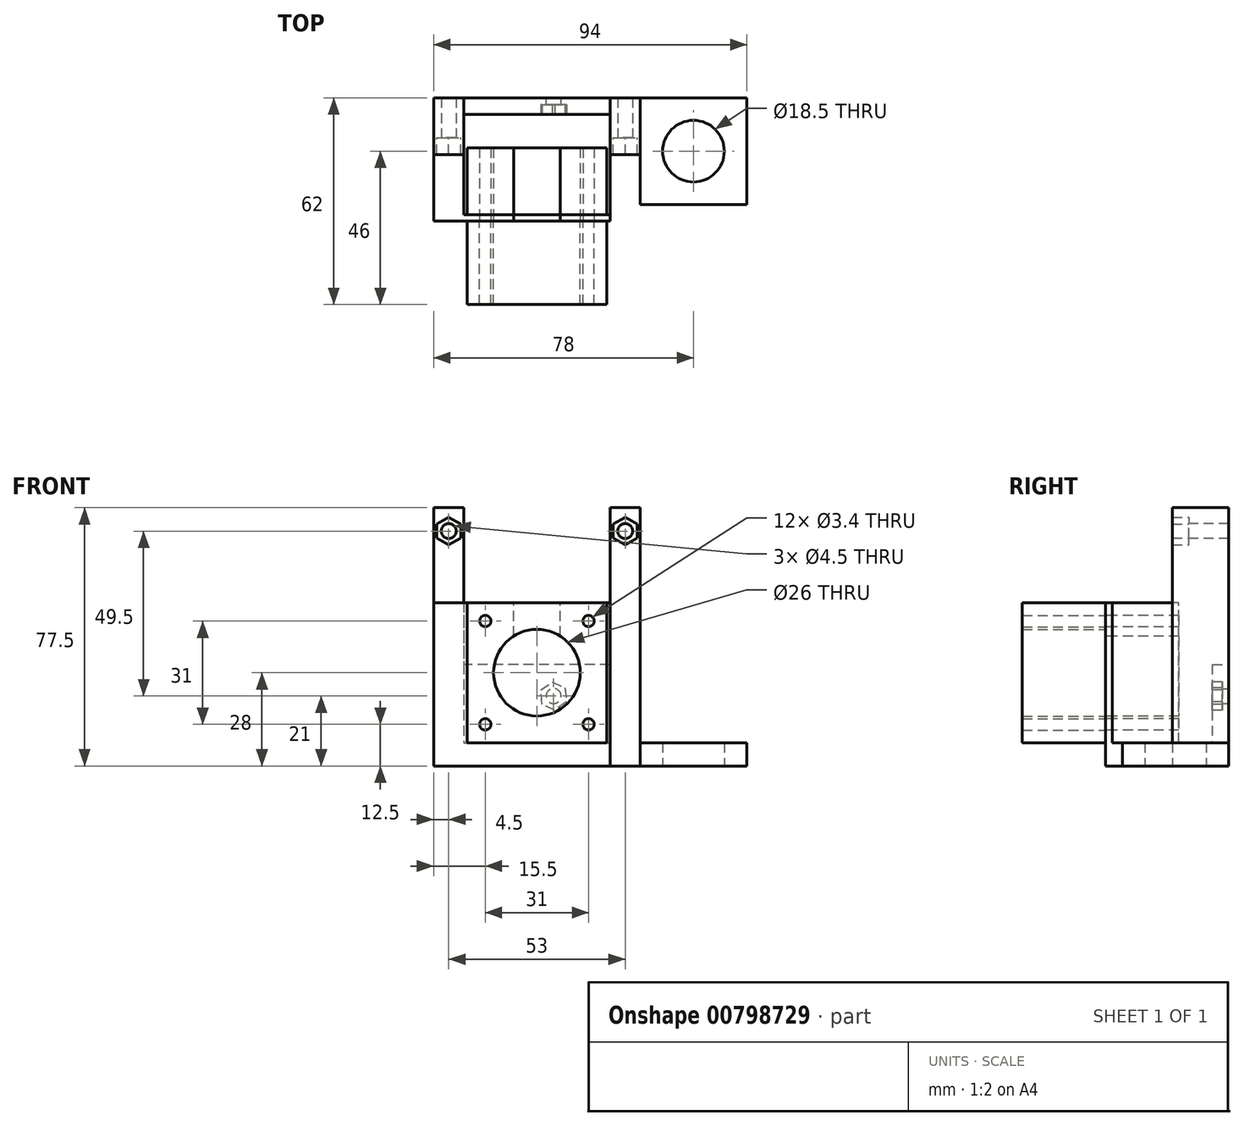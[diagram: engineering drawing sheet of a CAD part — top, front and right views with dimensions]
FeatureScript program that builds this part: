
annotation { "Feature Type Name" : "Feature", "Feature Type Description" : "" }
export const myFeature = defineFeature(function(context is Context, id is Id, definition is map)
    precondition{}
    {
        {
            assignVariable(context, id + "F0", {"name" : "MotorLength", "anyValue" : 20});
        }
        {
            var Q0;
            Q0=qCreatedBy(makeId("Front.planeOp"),FACE);
            var sketch = newSketch(context, id + "F1", { "sketchPlane" : qUnion([Q0])});
            skCircle(sketch, "E0", {"center": v(0, 0) * mm, "radius": 2.25 * mm});
            skCircle(sketch, "E1", {"center": v(-31.5, 49.5) * mm, "radius": 2.25 * mm});
            skCircle(sketch, "E2", {"center": v(21.5, 49.5) * mm, "radius": 2.25 * mm});
            skPoint(sketch, "E3", {"position": v(-36, 56.5) * mm});
            skPoint(sketch, "E4", {"position": v(-27, 56.5) * mm});
            skPoint(sketch, "E5", {"position": v(-27, -14) * mm});
            skLineSegment(sketch, "E6", {"start": v(-36, 56.5) * mm, "end": v(-27, 56.5) * mm});
            skLineSegment(sketch, "E7", {"start": v(-27, 56.5) * mm, "end": v(-27, -14) * mm});
            skLineSegment(sketch, "E8", {"start": v(-27, -14) * mm, "end": v(17, -14) * mm});
            skLineSegment(sketch, "E9", {"start": v(17, -14) * mm, "end": v(17, 56.5) * mm});
            skLineSegment(sketch, "E10", {"start": v(17, 56.5) * mm, "end": v(26, 56.5) * mm});
            skPoint(sketch, "E11", {"position": v(-36, -21) * mm});
            skLineSegment(sketch, "E12", {"start": v(-36, 56.5) * mm, "end": v(-36, -21) * mm});
            skLineSegment(sketch, "E13", {"start": v(-36, -21) * mm, "end": v(26, -21) * mm});
            skLineSegment(sketch, "E14", {"start": v(26, 56.5) * mm, "end": v(26, -21) * mm});
            skSolve(sketch);
        }
        {
            var Q0;
            Q0=makeQuery(id+"F1.imprint","IMPRINT",FACE,{"disambiguationData":[TD([[makeQuery(id+"F1.imprint","IMPRINT",EDGE,{"derivedFrom":sQuery(id+"F1.wireOp",EDGE,"E1")}),-1.0]])]});
            extrude(context, id + "F2", {"entities" : qUnion([Q0]), "oppositeDirection" : true, "depth" : 12 * mm});
        }
        {
            var Q0;
            Q0=makeQuery(id+"F2.opExtrude","CAP_FACE",FACE,{"disambiguationData":[OSD([sQuery(id+"F1.wireOp",EDGE,"E1"),sQuery(id+"F1.wireOp",EDGE,"E2"),sQuery(id+"F1.wireOp",EDGE,"E6"),sQuery(id+"F1.wireOp",EDGE,"E7"),sQuery(id+"F1.wireOp",EDGE,"E8"),sQuery(id+"F1.wireOp",EDGE,"E9"),sQuery(id+"F1.wireOp",EDGE,"E10"),sQuery(id+"F1.wireOp",EDGE,"E12"),sQuery(id+"F1.wireOp",EDGE,"E13"),sQuery(id+"F1.wireOp",EDGE,"E14")])],"isStart":true});
            var sketch = newSketch(context, id + "F3", { "sketchPlane" : qUnion([Q0])});
            skCircle(sketch, "E15.cCircle", {"center": v(-31.5, 49.5) * mm, "radius": 3.6 * mm, "construction": true});
            skLineSegment(sketch, "E15.0", {"start": v(-27.9, 51.58) * mm, "end": v(-27.9, 47.42) * mm});
            skLineSegment(sketch, "E15.1", {"start": v(-27.9, 47.42) * mm, "end": v(-31.5, 45.34) * mm});
            skLineSegment(sketch, "E15.2", {"start": v(-31.5, 45.34) * mm, "end": v(-35.1, 47.42) * mm});
            skLineSegment(sketch, "E15.3", {"start": v(-35.1, 47.42) * mm, "end": v(-35.1, 51.58) * mm});
            skLineSegment(sketch, "E15.4", {"start": v(-35.1, 51.58) * mm, "end": v(-31.5, 53.66) * mm});
            skLineSegment(sketch, "E15.5", {"start": v(-31.5, 53.66) * mm, "end": v(-27.9, 51.58) * mm});
            skPoint(sketch, "E15.0.midPoint", {"position": v(-27.9, 49.5) * mm});
            skCircle(sketch, "E16.cCircle", {"center": v(21.5, 49.5) * mm, "radius": 3.6 * mm, "construction": true});
            skLineSegment(sketch, "E16.0", {"start": v(25.1, 51.58) * mm, "end": v(25.1, 47.42) * mm});
            skLineSegment(sketch, "E16.1", {"start": v(25.1, 47.42) * mm, "end": v(21.5, 45.34) * mm});
            skLineSegment(sketch, "E16.2", {"start": v(21.5, 45.34) * mm, "end": v(17.9, 47.42) * mm});
            skLineSegment(sketch, "E16.3", {"start": v(17.9, 47.42) * mm, "end": v(17.9, 51.58) * mm});
            skLineSegment(sketch, "E16.4", {"start": v(17.9, 51.58) * mm, "end": v(21.5, 53.66) * mm});
            skLineSegment(sketch, "E16.5", {"start": v(21.5, 53.66) * mm, "end": v(25.1, 51.58) * mm});
            skPoint(sketch, "E16.0.midPoint", {"position": v(25.1, 49.5) * mm});
            skSolve(sketch);
        }
        {
            var Q0;
            Q0=makeQuery(id+"F3.imprint","IMPRINT",FACE,{"disambiguationData":[TD([[makeQuery(id+"F3.imprint","IMPRINT",EDGE,{"derivedFrom":sQuery(id+"F3.wireOp",EDGE,"E15.0")}),1.0]])]});
            extrude(context, id + "F4", {"entities" : qUnion([Q0]), "operationType" : NewBodyOperationType.ADD, "depth" : 5 * mm});
        }
        {
            var Q0;
            {var subQ0=sQuery(id+"F1.wireOp",EDGE,"E8");Q0=makeQuery(id+"F4.boolean.opBoolean","MERGE",FACE,{"derivedFrom":[makeQuery(id+"F2.opExtrude","SWEPT_FACE",FACE,{"disambiguationData":[OSD([subQ0])]}),makeQuery(id+"F4.opExtrude","SWEPT_FACE",FACE,{"disambiguationData":[OSD([subQ0])]})]});}
            var sketch = newSketch(context, id + "F5", { "sketchPlane" : qUnion([Q0])});
            skLineSegment(sketch, "E17.0", {"start": v(-27, 12) * mm, "end": v(17, 12) * mm});
            skPoint(sketch, "E18.oppositeSnap0", {"position": v(17, 3.5) * mm});
            skLineSegment(sketch, "E18.top", {"start": v(-27, -23) * mm, "end": v(17, -23) * mm});
            skLineSegment(sketch, "E18.left", {"start": v(-27, 12) * mm, "end": v(-27, -23) * mm});
            skLineSegment(sketch, "E18.right", {"start": v(17, 12) * mm, "end": v(17, -23) * mm});
            skLineSegment(sketch, "E19.top", {"start": v(-27, -25) * mm, "end": v(17, -25) * mm});
            skLineSegment(sketch, "E19.left", {"start": v(-27, -23) * mm, "end": v(-27, -25) * mm});
            skLineSegment(sketch, "E19.right", {"start": v(17, -23) * mm, "end": v(17, -25) * mm});
            skLineSegment(sketch, "E20.0", {"start": v(17, -5) * mm, "end": v(26, -5) * mm});
            skLineSegment(sketch, "E21.bottom", {"start": v(26, -5) * mm, "end": v(17, -5) * mm});
            skLineSegment(sketch, "E21.top", {"start": v(26, -25) * mm, "end": v(17, -25) * mm});
            skLineSegment(sketch, "E21.left", {"start": v(26, -5) * mm, "end": v(26, -25) * mm});
            skLineSegment(sketch, "E21.right", {"start": v(17, -5) * mm, "end": v(17, -25) * mm});
            skLineSegment(sketch, "E22.0", {"start": v(-36, -5) * mm, "end": v(-27, -5) * mm});
            skLineSegment(sketch, "E23.top", {"start": v(-36, -25) * mm, "end": v(-27, -25) * mm});
            skLineSegment(sketch, "E23.left", {"start": v(-36, -5) * mm, "end": v(-36, -25) * mm});
            skLineSegment(sketch, "E23.right", {"start": v(-27, -5) * mm, "end": v(-27, -25) * mm});
            skSolve(sketch);
        }
        {
            var Q0;
            {var subQ0=sQuery(id+"F5.wireOp",EDGE,"E18.top");Q0=makeQuery(id+"F5.imprint","IMPRINT",FACE,{"disambiguationData":[TD([[makeQuery(id+"F5.imprint","IMPRINT",EDGE,{"derivedFrom":subQ0}),1.0]])]});}
            var Q1;
            {var subQ0=sQuery(id+"F5.wireOp",EDGE,"E18.top");Q1=makeQuery(id+"F5.imprint","IMPRINT",FACE,{"disambiguationData":[TD([[makeQuery(id+"F5.imprint","IMPRINT",EDGE,{"derivedFrom":subQ0}),-1.0]])]});}
            var Q2;
            {var subQ1=sQuery(id+"F5.wireOp",EDGE,"E22.0");Q2=makeQuery(id+"F5.imprint","IMPRINT",FACE,{"disambiguationData":[TD([[makeQuery(id+"F5.imprint","IMPRINT",EDGE,{"derivedFrom":subQ1}),-1.0]])]});}
            var Q3;
            {var subQ1=sQuery(id+"F5.wireOp",EDGE,"E21.bottom");Q3=makeQuery(id+"F5.imprint","IMPRINT",FACE,{"disambiguationData":[TD([[makeQuery(id+"F5.imprint","IMPRINT",EDGE,{"derivedFrom":subQ1}),1.0]])]});}
            var Q4;
            {var subQ0=sQuery(id+"F1.wireOp",EDGE,"E13");Q4=makeQuery(id+"F4.boolean.opBoolean","MERGE",FACE,{"derivedFrom":[makeQuery(id+"F2.opExtrude","SWEPT_FACE",FACE,{"disambiguationData":[OSD([subQ0])]}),makeQuery(id+"F4.opExtrude","SWEPT_FACE",FACE,{"disambiguationData":[OSD([subQ0])]})]});}
            extrude(context, id + "F6", {"entities" : qUnion([Q0, Q1, Q2, Q3]), "operationType" : NewBodyOperationType.ADD, "endBound" : BoundingType.UP_TO_SURFACE, "oppositeDirection" : true, "endBoundEntityFace" : qUnion([Q4]), "depth" : 25 * mm});
        }
        {
            var Q0;
            {var subQ0=sQuery(id+"F5.wireOp",EDGE,"E18.top");Q0=makeQuery(id+"F5.imprint","IMPRINT",FACE,{"disambiguationData":[TD([[makeQuery(id+"F5.imprint","IMPRINT",EDGE,{"derivedFrom":subQ0}),-1.0]])]});}
            var Q1;
            {var subQ1=sQuery(id+"F5.wireOp",EDGE,"E22.0");Q1=makeQuery(id+"F5.imprint","IMPRINT",FACE,{"disambiguationData":[TD([[makeQuery(id+"F5.imprint","IMPRINT",EDGE,{"derivedFrom":subQ1}),-1.0]])]});}
            var Q2;
            {var subQ1=sQuery(id+"F5.wireOp",EDGE,"E21.bottom");Q2=makeQuery(id+"F5.imprint","IMPRINT",FACE,{"disambiguationData":[TD([[makeQuery(id+"F5.imprint","IMPRINT",EDGE,{"derivedFrom":subQ1}),1.0]])]});}
            extrude(context, id + "F7", {"entities" : qUnion([Q0, Q1, Q2]), "operationType" : NewBodyOperationType.ADD, "depth" : 42 * mm});
        }
        {
            var Q0;
            {var subQ0=sQuery(id+"F5.wireOp",EDGE,"E23.top");var subQ1=sQuery(id+"F5.wireOp",EDGE,"E21.top");var subQ2=sQuery(id+"F5.wireOp",EDGE,"E19.top");Q0=makeQuery(id+"F7.boolean.opBoolean","MERGE",FACE,{"derivedFrom":[makeQuery(id+"F6.opExtrude","SWEPT_FACE",FACE,{"disambiguationData":[OSD([subQ2,subQ1,subQ0])]}),makeQuery(id+"F7.opExtrude","SWEPT_FACE",FACE,{"disambiguationData":[OSD([subQ2,subQ1,subQ0])]})]});}
            var sketch = newSketch(context, id + "F8", { "sketchPlane" : qUnion([Q0])});
            skLineSegment(sketch, "E24.0", {"start": v(-26, -14) * mm, "end": v(16, -14) * mm});
            skPoint(sketch, "E25", {"position": v(-5, -14) * mm});
            skPoint(sketch, "E26", {"position": v(-26, -14) * mm});
            skPoint(sketch, "E27", {"position": v(16, -14) * mm});
            skPoint(sketch, "E28.orphan", {"position": v(-27, -14) * mm});
            skPoint(sketch, "E29.orphan", {"position": v(17, -14) * mm});
            skPoint(sketch, "E30", {"position": v(-26, 28) * mm});
            skPoint(sketch, "E31", {"position": v(16, 28) * mm});
            skLineSegment(sketch, "E32", {"start": v(-26, 28) * mm, "end": v(16, -14) * mm, "construction": true});
            skLineSegment(sketch, "E33", {"start": v(-26, -14) * mm, "end": v(16, 28) * mm, "construction": true});
            skPoint(sketch, "E34", {"position": v(-5, 7) * mm});
            skCircle(sketch, "E35", {"center": v(-5, 7) * mm, "radius": 13 * mm});
            skCircle(sketch, "E36", {"center": v(-20.5, 22.5) * mm, "radius": 1.7 * mm});
            skCircle(sketch, "E37.1.0", {"center": v(-20.5, -8.5) * mm, "radius": 1.7 * mm});
            skCircle(sketch, "E37.2.0", {"center": v(10.5, -8.5) * mm, "radius": 1.7 * mm});
            skCircle(sketch, "E37.3.0", {"center": v(10.5, 22.5) * mm, "radius": 1.7 * mm});
            skSolve(sketch);
        }
        {
            var Q0;
            Q0=makeQuery(id+"F8.imprint","IMPRINT",FACE,{"disambiguationData":[TD([[makeQuery(id+"F8.imprint","IMPRINT",EDGE,{"derivedFrom":sQuery(id+"F8.wireOp",EDGE,"E36")}),1.0]])]});
            var Q1;
            Q1=makeQuery(id+"F8.imprint","IMPRINT",FACE,{"disambiguationData":[TD([[makeQuery(id+"F8.imprint","IMPRINT",EDGE,{"derivedFrom":sQuery(id+"F8.wireOp",EDGE,"E35")}),1.0]])]});
            var Q2;
            Q2=makeQuery(id+"F8.imprint","IMPRINT",FACE,{"disambiguationData":[TD([[makeQuery(id+"F8.imprint","IMPRINT",EDGE,{"derivedFrom":sQuery(id+"F8.wireOp",EDGE,"E37.1.0")}),1.0]])]});
            var Q3;
            Q3=makeQuery(id+"F8.imprint","IMPRINT",FACE,{"disambiguationData":[TD([[makeQuery(id+"F8.imprint","IMPRINT",EDGE,{"derivedFrom":sQuery(id+"F8.wireOp",EDGE,"E37.2.0")}),1.0]])]});
            var Q4;
            Q4=makeQuery(id+"F8.imprint","IMPRINT",FACE,{"disambiguationData":[TD([[makeQuery(id+"F8.imprint","IMPRINT",EDGE,{"derivedFrom":sQuery(id+"F8.wireOp",EDGE,"E37.3.0")}),1.0]])]});
            var Q5;
            Q5=makeQuery(id+"F7.opExtrude","SWEPT_FACE",FACE,{"disambiguationData":[OSD([sQuery(id+"F5.wireOp",EDGE,"E18.top")])]});
            extrude(context, id + "F9", {"entities" : qUnion([Q0, Q1, Q2, Q3, Q4]), "operationType" : NewBodyOperationType.REMOVE, "endBound" : BoundingType.UP_TO_SURFACE, "oppositeDirection" : true, "endBoundEntityFace" : qUnion([Q5]), "depth" : 25 * mm});
        }
        {
            var Q0;
            Q0=makeQuery(id+"F7.opExtrude","CAP_FACE",FACE,{"disambiguationData":[OSD([sQuery(id+"F5.wireOp",EDGE,"E18.top"),sQuery(id+"F5.wireOp",EDGE,"E19.top"),sQuery(id+"F5.wireOp",EDGE,"E21.bottom"),sQuery(id+"F5.wireOp",EDGE,"E21.top"),sQuery(id+"F5.wireOp",EDGE,"E21.left"),sQuery(id+"F5.wireOp",EDGE,"E21.right"),sQuery(id+"F5.wireOp",EDGE,"E22.0"),sQuery(id+"F5.wireOp",EDGE,"E23.top"),sQuery(id+"F5.wireOp",EDGE,"E23.left"),sQuery(id+"F5.wireOp",EDGE,"E23.right")])],"isStart":false});
            var sketch = newSketch(context, id + "F10", { "sketchPlane" : qUnion([Q0])});
            skLineSegment(sketch, "E38", {"start": v(-5, -25) * mm, "end": v(-5, -23) * mm, "construction": true});
            skLineSegment(sketch, "E39", {"start": v(-5, -23) * mm, "end": v(-12, -23) * mm});
            skLineSegment(sketch, "E40", {"start": v(-5, -23) * mm, "end": v(2, -23) * mm});
            skLineSegment(sketch, "E41.bottom", {"start": v(-12, -23) * mm, "end": v(2, -23) * mm});
            skLineSegment(sketch, "E41.top", {"start": v(-12, -25) * mm, "end": v(2, -25) * mm});
            skLineSegment(sketch, "E41.left", {"start": v(-12, -23) * mm, "end": v(-12, -25) * mm});
            skLineSegment(sketch, "E41.right", {"start": v(2, -23) * mm, "end": v(2, -25) * mm});
            skSolve(sketch);
        }
        {
            var Q0;
            Q0=makeQuery(id+"F10.imprint","IMPRINT",FACE,{"disambiguationData":[TD([[makeQuery(id+"F10.imprint","IMPRINT",EDGE,{"derivedFrom":sQuery(id+"F10.wireOp",EDGE,"E41.top")}),1.0]])]});
            var Q1;
            Q1=makeQuery(id+"F9.boolean.opBoolean","COPY",FACE,{"derivedFrom":makeQuery(id+"F9.opExtrude","SWEPT_FACE",FACE,{"disambiguationData":[OSD([sQuery(id+"F8.wireOp",EDGE,"E35")])]})});
            extrude(context, id + "F11", {"entities" : qUnion([Q0]), "operationType" : NewBodyOperationType.REMOVE, "endBound" : BoundingType.UP_TO_SURFACE, "oppositeDirection" : true, "endBoundEntityFace" : qUnion([Q1]), "depth" : 25 * mm});
        }
        {
            var Q0;
            Q0=makeQuery(id+"F7.opExtrude","SWEPT_FACE",FACE,{"disambiguationData":[OSD([sQuery(id+"F5.wireOp",EDGE,"E18.top")])]});
            var sketch = newSketch(context, id + "F12", { "sketchPlane" : qUnion([Q0])});
            skLineSegment(sketch, "E42.0", {"start": v(26, -14) * mm, "end": v(-16, -14) * mm});
            skLineSegment(sketch, "E43", {"start": v(-16, -14) * mm, "end": v(-16, 28) * mm});
            skLineSegment(sketch, "E44", {"start": v(-16, 28) * mm, "end": v(26, 28) * mm});
            skLineSegment(sketch, "E45", {"start": v(26, 28) * mm, "end": v(26, -14) * mm});
            skSolve(sketch);
        }
        {
            var Q0;
            Q0=makeQuery(id+"F12.imprint","IMPRINT",FACE,{"disambiguationData":[TD([[makeQuery(id+"F12.imprint","IMPRINT",EDGE,{"derivedFrom":sQuery(id+"F12.wireOp",EDGE,"E42.0")}),-1.0]])]});
            var Q1;
            {var subQ2=sQuery(id+"F5.wireOp",EDGE,"E18.top");Q1=makeQuery(id+"F12.imprint","IMPRINT",FACE,{"disambiguationData":[TD([[makeQuery(id+"F12.imprint","IMPRINT",EDGE,{"derivedFrom":makeQuery(id+"F9.boolean.opBoolean","COPY",EDGE,{"derivedFrom":makeQuery(id+"F9.opExtrude","TWEAK_EDGE",EDGE,{"derivedFrom":[makeQuery(id+"F7.opExtrude","SWEPT_FACE",FACE,{"disambiguationData":[OSD([subQ2])]}),makeQuery(id+"F8.imprint","IMPRINT",EDGE,{"derivedFrom":sQuery(id+"F8.wireOp",EDGE,"E35")})]})})}),-1.0]])]});}
            var Q2;
            Q2=makeQuery(id+"F12.imprint","IMPRINT",FACE,{"disambiguationData":[TD([[makeQuery(id+"F12.imprint","IMPRINT",EDGE,{"derivedFrom":makeQuery(id+"F9.boolean.opBoolean","COPY",EDGE,{"derivedFrom":makeQuery(id+"F9.opExtrude","TWEAK_EDGE",EDGE,{"derivedFrom":[makeQuery(id+"F7.opExtrude","SWEPT_FACE",FACE,{"disambiguationData":[OSD([sQuery(id+"F5.wireOp",EDGE,"E18.top")])]}),makeQuery(id+"F8.imprint","IMPRINT",EDGE,{"derivedFrom":sQuery(id+"F8.wireOp",EDGE,"E36")})]})})}),-1.0]])]});
            var Q3;
            Q3=makeQuery(id+"F12.imprint","IMPRINT",FACE,{"disambiguationData":[TD([[makeQuery(id+"F12.imprint","IMPRINT",EDGE,{"derivedFrom":makeQuery(id+"F9.boolean.opBoolean","COPY",EDGE,{"derivedFrom":makeQuery(id+"F9.opExtrude","TWEAK_EDGE",EDGE,{"derivedFrom":[makeQuery(id+"F7.opExtrude","SWEPT_FACE",FACE,{"disambiguationData":[OSD([sQuery(id+"F5.wireOp",EDGE,"E18.top")])]}),makeQuery(id+"F8.imprint","IMPRINT",EDGE,{"derivedFrom":sQuery(id+"F8.wireOp",EDGE,"E37.3.0")})]})})}),-1.0]])]});
            var Q4;
            Q4=makeQuery(id+"F12.imprint","IMPRINT",FACE,{"disambiguationData":[TD([[makeQuery(id+"F12.imprint","IMPRINT",EDGE,{"derivedFrom":makeQuery(id+"F9.boolean.opBoolean","COPY",EDGE,{"derivedFrom":makeQuery(id+"F9.opExtrude","TWEAK_EDGE",EDGE,{"derivedFrom":[makeQuery(id+"F7.opExtrude","SWEPT_FACE",FACE,{"disambiguationData":[OSD([sQuery(id+"F5.wireOp",EDGE,"E18.top")])]}),makeQuery(id+"F8.imprint","IMPRINT",EDGE,{"derivedFrom":sQuery(id+"F8.wireOp",EDGE,"E37.2.0")})]})})}),-1.0]])]});
            var Q5;
            Q5=makeQuery(id+"F12.imprint","IMPRINT",FACE,{"disambiguationData":[TD([[makeQuery(id+"F12.imprint","IMPRINT",EDGE,{"derivedFrom":makeQuery(id+"F9.boolean.opBoolean","COPY",EDGE,{"derivedFrom":makeQuery(id+"F9.opExtrude","TWEAK_EDGE",EDGE,{"derivedFrom":[makeQuery(id+"F7.opExtrude","SWEPT_FACE",FACE,{"disambiguationData":[OSD([sQuery(id+"F5.wireOp",EDGE,"E18.top")])]}),makeQuery(id+"F8.imprint","IMPRINT",EDGE,{"derivedFrom":sQuery(id+"F8.wireOp",EDGE,"E37.1.0")})]})})}),-1.0]])]});
            extrude(context, id + "F13", {"entities" : qUnion([Q0, Q1, Q2, Q3, Q4, Q5]), "depth" : (getVariable(context, 'MotorLength')) * mm});
        }
        {
            var Q0;
            Q0=makeQuery(id+"F8.imprint","IMPRINT",FACE,{"disambiguationData":[TD([[makeQuery(id+"F8.imprint","IMPRINT",EDGE,{"derivedFrom":sQuery(id+"F8.wireOp",EDGE,"E35")}),-1.0]])]});
            var sketch = newSketch(context, id + "F14", { "sketchPlane" : qUnion([Q0])});
            skLineSegment(sketch, "E46.0", {"start": v(-26, 28) * mm, "end": v(16, -14) * mm, "construction": true});
            skLineSegment(sketch, "E47.0", {"start": v(-26, -14) * mm, "end": v(16, 28) * mm, "construction": true});
            skLineSegment(sketch, "E48.bottom", {"start": v(-26, 28) * mm, "end": v(16, 28) * mm});
            skLineSegment(sketch, "E48.top", {"start": v(-26, -14) * mm, "end": v(16, -14) * mm});
            skLineSegment(sketch, "E48.left", {"start": v(-26, 28) * mm, "end": v(-26, -14) * mm});
            skLineSegment(sketch, "E48.right", {"start": v(16, 28) * mm, "end": v(16, -14) * mm});
            skSolve(sketch);
        }
        {
            var Q0;
            Q0=makeQuery(id+"F14.imprint","IMPRINT",FACE,{"disambiguationData":[TD([[makeQuery(id+"F14.imprint","IMPRINT",EDGE,{"derivedFrom":sQuery(id+"F14.wireOp",EDGE,"E48.bottom")}),-1.0]])]});
            var Q1;
            Q1=makeQuery(id+"F8.imprint","IMPRINT",FACE,{"disambiguationData":[TD([[makeQuery(id+"F8.imprint","IMPRINT",EDGE,{"derivedFrom":sQuery(id+"F8.wireOp",EDGE,"E36")}),1.0]])]});
            var Q2;
            Q2=makeQuery(id+"F8.imprint","IMPRINT",FACE,{"disambiguationData":[TD([[makeQuery(id+"F8.imprint","IMPRINT",EDGE,{"derivedFrom":sQuery(id+"F8.wireOp",EDGE,"E35")}),1.0]])]});
            var Q3;
            Q3=makeQuery(id+"F8.imprint","IMPRINT",FACE,{"disambiguationData":[TD([[makeQuery(id+"F8.imprint","IMPRINT",EDGE,{"derivedFrom":sQuery(id+"F8.wireOp",EDGE,"E37.1.0")}),1.0]])]});
            var Q4;
            Q4=makeQuery(id+"F8.imprint","IMPRINT",FACE,{"disambiguationData":[TD([[makeQuery(id+"F8.imprint","IMPRINT",EDGE,{"derivedFrom":sQuery(id+"F8.wireOp",EDGE,"E37.3.0")}),1.0]])]});
            var Q5;
            Q5=makeQuery(id+"F8.imprint","IMPRINT",FACE,{"disambiguationData":[TD([[makeQuery(id+"F8.imprint","IMPRINT",EDGE,{"derivedFrom":sQuery(id+"F8.wireOp",EDGE,"E37.2.0")}),1.0]])]});
            extrude(context, id + "F15", {"entities" : qUnion([Q0, Q1, Q2, Q3, Q4, Q5]), "depth" : 25 * mm});
        }
        {
            var Q0;
            {var subQ0=sQuery(id+"F1.wireOp",EDGE,"E13");Q0=makeQuery(id+"F6.boolean.opBoolean","MERGE",FACE,{"derivedFrom":[makeQuery(id+"F4.boolean.opBoolean","MERGE",FACE,{"derivedFrom":[makeQuery(id+"F2.opExtrude","SWEPT_FACE",FACE,{"disambiguationData":[OSD([subQ0])]}),makeQuery(id+"F4.opExtrude","SWEPT_FACE",FACE,{"disambiguationData":[OSD([subQ0])]})]}),makeQuery(id+"F6.opExtrude","CAP_FACE",FACE,{"disambiguationData":[OSD([subQ0])],"isStart":false})]});}
            var sketch = newSketch(context, id + "F16", { "sketchPlane" : qUnion([Q0])});
            skLineSegment(sketch, "E49.bottom", {"start": v(26, -12) * mm, "end": v(58, -12) * mm});
            skLineSegment(sketch, "E49.top", {"start": v(26, 20) * mm, "end": v(58, 20) * mm});
            skLineSegment(sketch, "E49.left", {"start": v(26, -12) * mm, "end": v(26, 20) * mm});
            skLineSegment(sketch, "E49.right", {"start": v(58, -12) * mm, "end": v(58, 20) * mm});
            skCircle(sketch, "E50", {"center": v(42, 4) * mm, "radius": 9.25 * mm});
            skPoint(sketch, "E50.centerSnap0", {"position": v(42, -12) * mm});
            skPoint(sketch, "E50.centerSnap1", {"position": v(26, 4) * mm});
            skLineSegment(sketch, "E51.0", {"start": v(-26, 50) * mm, "end": v(-26, 25) * mm, "construction": true});
            skLineSegment(sketch, "E52.0", {"start": v(-26, 25) * mm, "end": v(16, 25) * mm, "construction": true});
            skLineSegment(sketch, "E53", {"start": v(-5, 25) * mm, "end": v(-5, 50) * mm, "construction": true});
            skLineSegment(sketch, "E54", {"start": v(6.1, 25) * mm, "end": v(6.1, 50) * mm, "construction": true});
            skPoint(sketch, "E55", {"position": v(6.1, 37.5) * mm});
            skSolve(sketch);
        }
        {
            var Q0;
            Q0=qSketchRegion(id+"F16",true);
            var Q1;
            {var subQ0=sQuery(id+"F1.wireOp",EDGE,"E8");Q1=makeQuery(id+"F6.boolean.opBoolean","MERGE",FACE,{"derivedFrom":[makeQuery(id+"F4.boolean.opBoolean","MERGE",FACE,{"derivedFrom":[makeQuery(id+"F2.opExtrude","SWEPT_FACE",FACE,{"disambiguationData":[OSD([subQ0])]}),makeQuery(id+"F4.opExtrude","SWEPT_FACE",FACE,{"disambiguationData":[OSD([subQ0])]})]}),makeQuery(id+"F6.opExtrude","CAP_FACE",FACE,{"disambiguationData":[OSD([subQ0,sQuery(id+"F5.wireOp",EDGE,"E19.top"),sQuery(id+"F5.wireOp",EDGE,"E21.bottom"),sQuery(id+"F5.wireOp",EDGE,"E21.top"),sQuery(id+"F5.wireOp",EDGE,"E21.left"),sQuery(id+"F5.wireOp",EDGE,"E22.0"),sQuery(id+"F5.wireOp",EDGE,"E23.top"),sQuery(id+"F5.wireOp",EDGE,"E23.left")])],"isStart":true})]});}
            extrude(context, id + "F17", {"entities" : qUnion([Q0]), "endBound" : BoundingType.UP_TO_SURFACE, "oppositeDirection" : true, "endBoundEntityFace" : qUnion([Q1]), "depth" : 25 * mm});
        }
        {
            var Q0;
            Q0=makeQuery(id+"F2.opExtrude","CAP_FACE",FACE,{"disambiguationData":[OSD([sQuery(id+"F1.wireOp",EDGE,"E1"),sQuery(id+"F1.wireOp",EDGE,"E2"),sQuery(id+"F1.wireOp",EDGE,"E6"),sQuery(id+"F1.wireOp",EDGE,"E7"),sQuery(id+"F1.wireOp",EDGE,"E8"),sQuery(id+"F1.wireOp",EDGE,"E9"),sQuery(id+"F1.wireOp",EDGE,"E10"),sQuery(id+"F1.wireOp",EDGE,"E12"),sQuery(id+"F1.wireOp",EDGE,"E13"),sQuery(id+"F1.wireOp",EDGE,"E14")])],"isStart":false});
            var sketch = newSketch(context, id + "F18", { "sketchPlane" : qUnion([Q0])});
            skLineSegment(sketch, "E56.bottom", {"start": v(-17, -14) * mm, "end": v(27, -14) * mm});
            skLineSegment(sketch, "E56.top", {"start": v(-17, 9.47) * mm, "end": v(27, 9.47) * mm});
            skLineSegment(sketch, "E56.left", {"start": v(-17, -14) * mm, "end": v(-17, 9.47) * mm});
            skLineSegment(sketch, "E56.right", {"start": v(27, -14) * mm, "end": v(27, 9.47) * mm});
            skCircle(sketch, "E57.0", {"center": v(0, 0) * mm, "radius": 2.25 * mm});
            skSolve(sketch);
        }
        {
            var Q0;
            Q0 = qSketchRegion(id + "F18", true);
            extrude(context, id + "F19", {"entities" : qUnion([Q0]), "operationType" : NewBodyOperationType.ADD, "depth" : -5 * mm, "offsetDistance" : 25 * mm});
        }
        {
            var Q0;
            Q0=makeQuery(id+"F19.opExtrude","CAP_FACE",FACE,{"disambiguationData":[OSD([sQuery(id+"F18.wireOp",EDGE,"E56.bottom"),sQuery(id+"F18.wireOp",EDGE,"E56.top"),sQuery(id+"F18.wireOp",EDGE,"E56.left"),sQuery(id+"F18.wireOp",EDGE,"E56.right"),sQuery(id+"F18.wireOp",EDGE,"E57.0")])],"isStart":false});
            var sketch = newSketch(context, id + "F20", { "sketchPlane" : qUnion([Q0])});
            skCircle(sketch, "E58.cCircle", {"center": v(0, 0) * mm, "radius": 3.68 * mm, "construction": true});
            skLineSegment(sketch, "E58.0", {"start": v(-3.87, 1.76) * mm, "end": v(-0.41, 4.23) * mm});
            skLineSegment(sketch, "E58.1", {"start": v(-0.41, 4.23) * mm, "end": v(3.46, 2.47) * mm});
            skLineSegment(sketch, "E58.2", {"start": v(3.46, 2.47) * mm, "end": v(3.87, -1.76) * mm});
            skLineSegment(sketch, "E58.3", {"start": v(3.87, -1.76) * mm, "end": v(0.41, -4.23) * mm});
            skLineSegment(sketch, "E58.4", {"start": v(0.41, -4.23) * mm, "end": v(-3.46, -2.47) * mm});
            skLineSegment(sketch, "E58.5", {"start": v(-3.46, -2.47) * mm, "end": v(-3.87, 1.76) * mm});
            skPoint(sketch, "E58.0.midPoint", {"position": v(-2.14, 3) * mm});
            skSolve(sketch);
        }
        {
            var Q0;
            Q0=makeQuery(id+"F20.imprint","IMPRINT",FACE,{"disambiguationData":[TD([[makeQuery(id+"F20.imprint","IMPRINT",EDGE,{"derivedFrom":sQuery(id+"F20.wireOp",EDGE,"E58.0")}),-1.0]])]});
            extrude(context, id + "F21", {"entities" : qUnion([Q0]), "operationType" : NewBodyOperationType.REMOVE, "oppositeDirection" : true, "depth" : 3 * mm, "offsetDistance" : 25 * mm});
        }
    });
